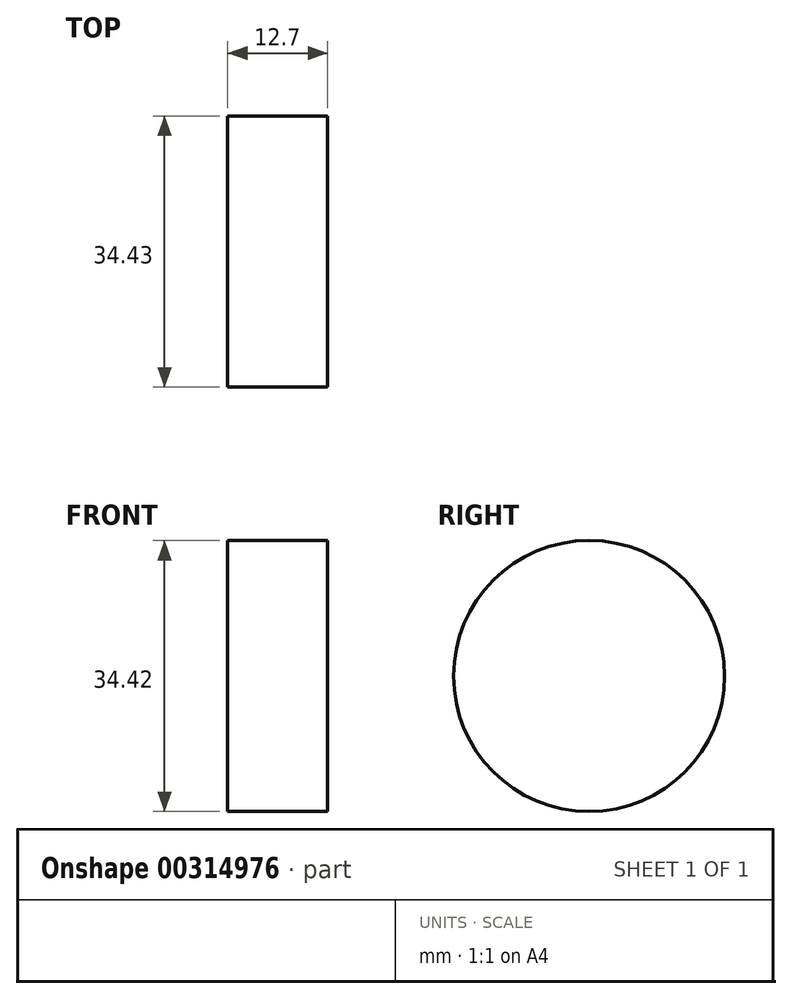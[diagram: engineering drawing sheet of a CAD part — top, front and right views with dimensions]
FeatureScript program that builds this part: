
annotation { "Feature Type Name" : "Feature", "Feature Type Description" : "" }
export const myFeature = defineFeature(function(context is Context, id is Id, definition is map)
    precondition{}
    {
        {
            var Q0;
            Q0=qCreatedBy(makeId("Right.planeOp"),FACE);
            var sketch = newSketch(context, id + "F0", { "sketchPlane" : qUnion([Q0])});
            skCircle(sketch, "E0", {"center": v(-45.7, 50.09) * mm, "radius": 17.21 * mm});
            skSolve(sketch);
        }
        {
            var Q0;
            Q0 = qSketchRegion(id + "F0", true);
            extrude(context, id + "F1", {"entities" : qUnion([Q0]), "depth" : 12.7 * mm});
        }
    });
